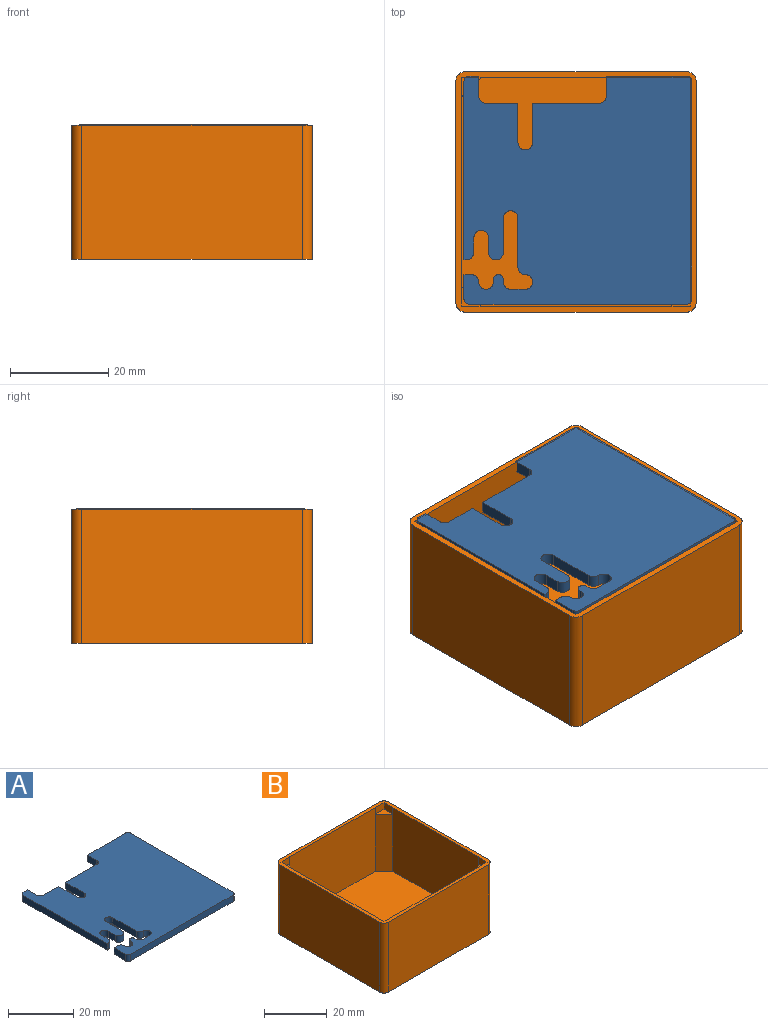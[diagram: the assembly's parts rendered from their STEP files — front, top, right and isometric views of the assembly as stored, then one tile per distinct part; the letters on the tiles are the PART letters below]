
ASSEMBLY  parts=2 mates=1
PART A: 40 faces, bbox 46.4x46.4x2.4 mm
  f0: plane 5x2.4mm, normal (-1,0,0), area 12mm2, adj f2,f8,f10,f23
  f1: plane 6.5x2.4mm, normal (0,1,0), area 15.6mm2, adj f2,f8,f16,f37
  f2: plane 46.4x46.4mm, normal (0,0,-1), area 1876mm2, adj f0,f1,f3,f4,f5,f6,f7,f9
  f3: plane 16.4x2.4mm, normal (0,1,0), area 39.4mm2, adj f2,f8,f12,f15
  f4: plane 2.4x2mm, normal (0,1,0), area 4.8mm2, adj f2,f8,f9,f13
  f5: plane 36.4x2.4mm, normal (-1,0,0), area 87.4mm2, adj f2,f8,f9,f22
  f6: plane 44.4x2.4mm, normal (0,-1,0), area 106.6mm2, adj f2,f8,f10,f11
  f7: plane 44.4x2.4mm, normal (1,0,0), area 106.6mm2, adj f2,f8,f11,f12
  f8: plane 46.4x46.4mm, normal (0,0,1), area 1876mm2, adj f0,f1,f3,f4,f5,f6,f7,f9
  f9: cylinder r=1mm len=2.4mm, axis (0,0,1), area 3.8mm2, adj f2,f4,f5,f8
  f10: cylinder r=1mm len=2.4mm, axis (0,0,-1), area 3.8mm2, adj f0,f2,f6,f8
  f11: cylinder r=1mm len=2.4mm, axis (0,0,1), area 3.8mm2, adj f2,f6,f7,f8
  f12: cylinder r=1mm len=2.4mm, axis (0,0,-1), area 3.8mm2, adj f2,f3,f7,f8
  f13: plane 4x2.4mm, normal (1,0,0), area 9.6mm2, adj f2,f4,f8,f37
  f14: plane 13.5x2.4mm, normal (0,1,0), area 32.4mm2, adj f2,f8,f17,f38
  f15: plane 4x2.4mm, normal (-1,0,0), area 9.6mm2, adj f2,f3,f8,f38
  f16: plane 8x2.4mm, normal (1,0,0), area 19.2mm2, adj f1,f2,f8,f36
  f17: plane 8x2.4mm, normal (-1,0,0), area 19.2mm2, adj f2,f8,f14,f36
  f18: plane 10x2.4mm, normal (-1,0,0), area 24mm2, adj f2,f8,f34,f35
  f19: plane 7x2.4mm, normal (1,0,0), area 16.8mm2, adj f2,f8,f27,f35
  f20: plane 3x2.4mm, normal (-1,0,0), area 7.2mm2, adj f2,f8,f27,f28
  f21: plane 3x2.4mm, normal (1,0,0), area 7.2mm2, adj f2,f8,f28,f29
  f22: plane 2.4x0.5mm, normal (0,-1,0), area 1.2mm2, adj f2,f5,f8,f29
  f23: plane 2.4x1.5mm, normal (0,1,0), area 3.6mm2, adj f0,f2,f8,f31
  f24: plane 2.4x0.5mm, normal (-1,0,0), area 1.2mm2, adj f2,f8,f30,f39
  f25: plane 2.4x0.5mm, normal (1,0,0), area 1.2mm2, adj f2,f8,f32,f39
  f26: plane 3x2.4mm, normal (0,1,0), area 7.2mm2, adj f2,f8,f32,f33
  f27: cylinder r=1.5mm len=3mm, axis (0,0,-1), area 11.3mm2, adj f2,f8,f19,f20
  f28: cylinder r=1.5mm len=3mm, axis (0,0,1), area 11.3mm2, adj f2,f8,f20,f21
  f29: cylinder r=1.5mm len=2.4mm, axis (0,0,-1), area 5.7mm2, adj f2,f8,f21,f22
  f30: cylinder r=1.5mm len=3mm, axis (0,0,-1), area 11.3mm2, adj f2,f8,f24,f31
  f31: cylinder r=1.5mm len=2.4mm, axis (0,0,-1), area 5.7mm2, adj f2,f8,f23,f30
  f32: cylinder r=1.5mm len=2.4mm, axis (0,0,1), area 5.7mm2, adj f2,f8,f25,f26
  f33: cylinder r=1.5mm len=3mm, axis (0,0,-1), area 11.3mm2, adj f2,f8,f26,f34
  f34: cylinder r=1.5mm len=2.4mm, axis (0,0,-1), area 5.7mm2, adj f2,f8,f18,f33
  f35: cylinder r=1.5mm len=3mm, axis (0,0,1), area 11.3mm2, adj f2,f8,f18,f19
  f36: cylinder r=1.5mm len=3mm, axis (0,0,1), area 11.3mm2, adj f2,f8,f16,f17
  f37: cylinder r=1.5mm len=2.4mm, axis (0,0,-1), area 5.7mm2, adj f1,f2,f8,f13
  f38: cylinder r=1.5mm len=2.4mm, axis (0,0,1), area 5.7mm2, adj f2,f8,f14,f15
  f39: cylinder r=1mm len=2.4mm, axis (0,0,-1), area 7.5mm2, adj f2,f8,f24,f25
PART B: 31 faces, bbox 49x49x27.3 mm
  f0: plane 49x49mm, normal (0,0,1), area 227.6mm2, adj f1,f2,f3,f4,f5,f6,f8,f9
  f1: plane 24.9x4mm, normal (-0.71,-0.71,0), area 126.5mm2, adj f0,f8,f9,f12,f25,f26,f27
  f2: plane 24.9x4mm, normal (-0.71,0.71,0), area 126.5mm2, adj f0,f8,f11,f12,f19,f20,f21
  f3: plane 45x27.3mm, normal (0,1,0), area 1228.5mm2, adj f0,f7,f13,f16
  f4: plane 45x27.3mm, normal (-1,0,0), area 1228.5mm2, adj f0,f7,f13,f14
  f5: plane 45x27.3mm, normal (0,-1,0), area 1228.5mm2, adj f0,f7,f14,f15
  f6: plane 45x27.3mm, normal (1,0,0), area 1228.5mm2, adj f0,f7,f15,f16
  f7: plane 49x49mm, normal (0,0,-1), area 2397.6mm2, adj f3,f4,f5,f6,f13,f14,f15,f16
  f8: plane 38.6x24.9mm, normal (-1,0,0), area 961.1mm2, adj f0,f1,f2,f12
  f9: plane 38.6x24.9mm, normal (0,-1,0), area 961.1mm2, adj f0,f1,f12,f17
  f10: plane 38.6x24.9mm, normal (1,0,0), area 961.1mm2, adj f0,f12,f17,f18
  f11: plane 38.6x24.9mm, normal (0,1,0), area 961.1mm2, adj f0,f2,f12,f18
  f12: plane 46.6x46.6mm, normal (0,0,1), area 2139.6mm2, adj f1,f2,f8,f9,f10,f11,f17,f18
  f13: cylinder r=2mm len=27.3mm, axis (0,0,1), area 85.8mm2, adj f0,f3,f4,f7
  f14: cylinder r=2mm len=27.3mm, axis (0,0,-1), area 85.8mm2, adj f0,f4,f5,f7
  f15: cylinder r=2mm len=27.3mm, axis (0,0,1), area 85.8mm2, adj f0,f5,f6,f7
  f16: cylinder r=2mm len=27.3mm, axis (0,0,-1), area 85.8mm2, adj f0,f3,f6,f7
  f17: plane 24.9x4mm, normal (0.71,-0.71,0), area 126.5mm2, adj f0,f9,f10,f12,f28,f29,f30
  f18: plane 24.9x4mm, normal (0.71,0.71,0), area 126.5mm2, adj f0,f10,f11,f12,f22,f23,f24
  f19: plane 3.9x3.9mm, normal (0,0,1), area 7.6mm2, adj f2,f20,f21
  f20: plane 3.9x2.6mm, normal (0,1,0), area 10.1mm2, adj f0,f2,f19,f21
  f21: plane 3.9x2.6mm, normal (-1,0,0), area 10.1mm2, adj f0,f2,f19,f20
  f22: plane 3.9x3.9mm, normal (0,0,1), area 7.6mm2, adj f18,f23,f24
  f23: plane 3.9x2.6mm, normal (0,1,0), area 10.1mm2, adj f0,f18,f22,f24
  f24: plane 3.9x2.6mm, normal (1,0,0), area 10.1mm2, adj f0,f18,f22,f23
  f25: plane 3.9x3.9mm, normal (0,0,1), area 7.6mm2, adj f1,f26,f27
  f26: plane 3.9x2.6mm, normal (0,-1,0), area 10.1mm2, adj f0,f1,f25,f27
  f27: plane 3.9x2.6mm, normal (-1,0,0), area 10.1mm2, adj f0,f1,f25,f26
  f28: plane 3.9x2.6mm, normal (0,-1,0), area 10.1mm2, adj f0,f17,f29,f30
  f29: plane 3.9x2.6mm, normal (1,0,0), area 10.1mm2, adj f0,f17,f28,f30
  f30: plane 3.9x3.9mm, normal (0,0,1), area 7.6mm2, adj f17,f28,f29
PLACE A t=(-75.15,-2.8,25)mm
PLACE B at identity fixed
MATE slider B.f12 <-> A.f8  axis (0,0,1) through (-41.84,40.26,2.4)mm
